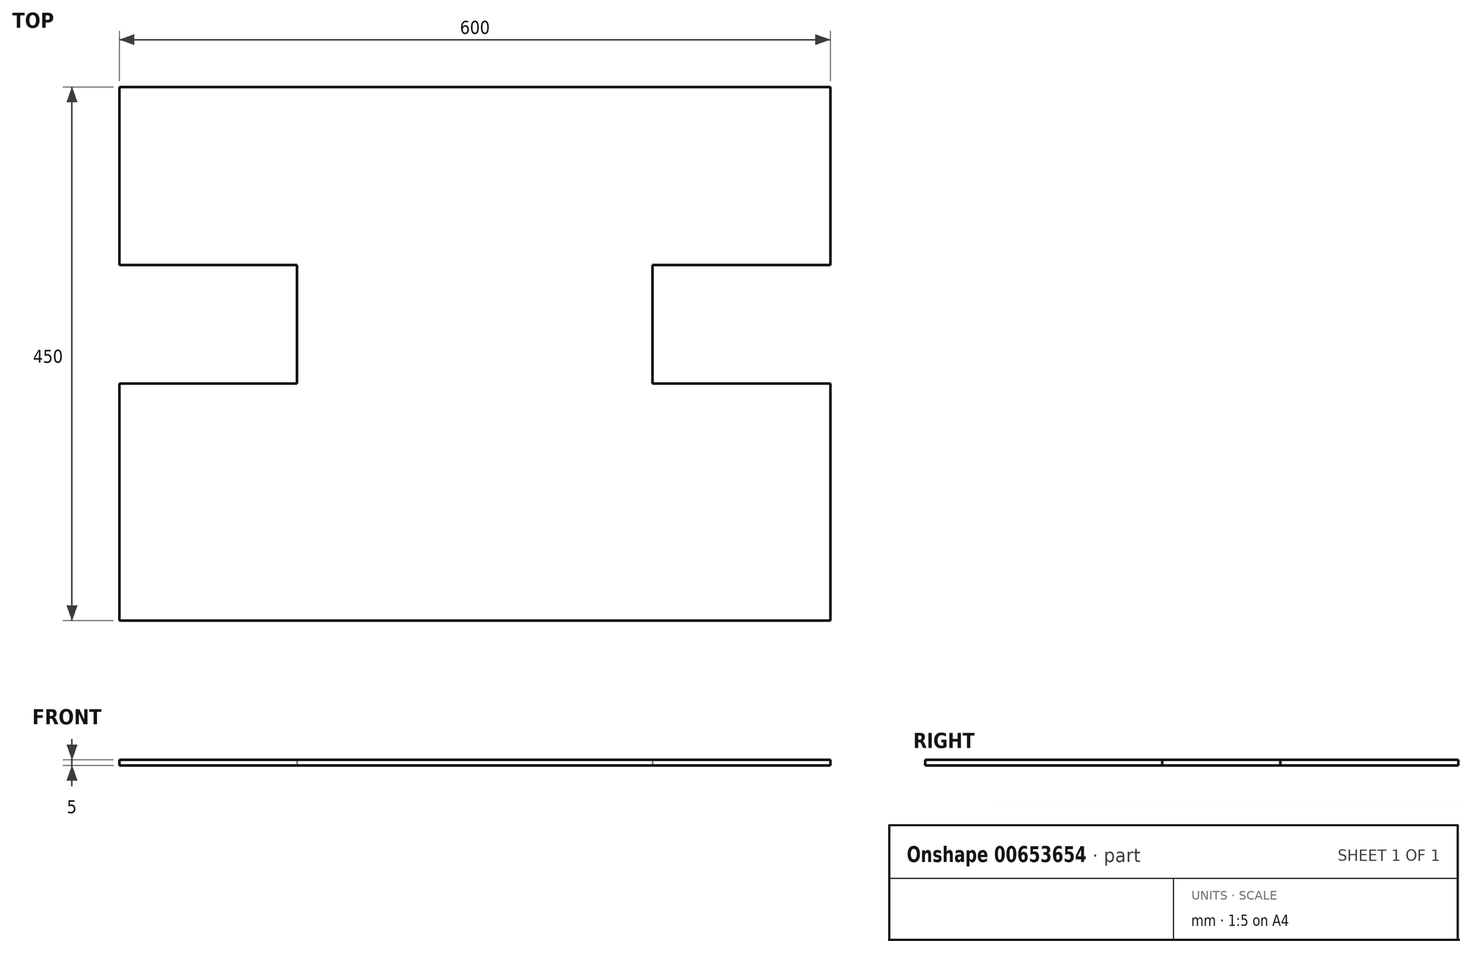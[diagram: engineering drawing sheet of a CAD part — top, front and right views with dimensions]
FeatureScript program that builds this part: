
annotation { "Feature Type Name" : "Feature", "Feature Type Description" : "" }
export const myFeature = defineFeature(function(context is Context, id is Id, definition is map)
    precondition{}
    {
        {
            var Q0;
            Q0=qCreatedBy(makeId("Top.planeOp"),FACE);
            var sketch = newSketch(context, id + "F0", { "sketchPlane" : qUnion([Q0])});
            skLineSegment(sketch, "E0.bottom", {"start": v(0, 0) * mm, "end": v(600, 0) * mm});
            skLineSegment(sketch, "E0.top", {"start": v(0, 450) * mm, "end": v(600, 450) * mm});
            skLineSegment(sketch, "E0.left", {"start": v(0, 0) * mm, "end": v(0, 450) * mm});
            skLineSegment(sketch, "E0.right", {"start": v(600, 0) * mm, "end": v(600, 450) * mm});
            skLineSegment(sketch, "E1", {"start": v(0, 0) * mm, "end": v(150, -200) * mm});
            skLineSegment(sketch, "E2", {"start": v(150, -200) * mm, "end": v(450, -200) * mm});
            skLineSegment(sketch, "E3", {"start": v(450, -200) * mm, "end": v(600, 0) * mm});
            skLineSegment(sketch, "E4.bottom", {"start": v(0, 300) * mm, "end": v(150, 300) * mm});
            skLineSegment(sketch, "E4.top", {"start": v(0, 200) * mm, "end": v(150, 200) * mm});
            skLineSegment(sketch, "E4.left", {"start": v(0, 300) * mm, "end": v(0, 200) * mm});
            skLineSegment(sketch, "E4.right", {"start": v(150, 300) * mm, "end": v(150, 200) * mm});
            skLineSegment(sketch, "E5.bottom", {"start": v(600, 200) * mm, "end": v(450, 200) * mm});
            skLineSegment(sketch, "E5.top", {"start": v(600, 300) * mm, "end": v(450, 300) * mm});
            skLineSegment(sketch, "E5.left", {"start": v(600, 200) * mm, "end": v(600, 300) * mm});
            skLineSegment(sketch, "E5.right", {"start": v(450, 200) * mm, "end": v(450, 300) * mm});
            skSolve(sketch);
        }
        {
            var Q0;
            {var subQ6=sQuery(id+"F0.wireOp",EDGE,"E0.bottom");Q0=makeQuery(id+"F0.imprint","IMPRINT",FACE,{"disambiguationData":[TD([[makeQuery(id+"F0.imprint","IMPRINT",EDGE,{"derivedFrom":subQ6}),1.0]])]});}
            var Q1;
            Q1=makeQuery(id+"F0.imprint","IMPRINT",FACE,{"disambiguationData":[TD([[makeQuery(id+"F0.imprint","IMPRINT",EDGE,{"derivedFrom":sQuery(id+"F0.wireOp",EDGE,"E0.bottom")}),-1.0]])]});
            extrude(context, id + "F1", {"entities" : qUnion([Q0, Q1]), "depth" : 5 * mm, "offsetDistance" : 25 * mm});
        }
        {
            var Q0;
            Q0=makeQuery(id+"F1.opExtrude","CAP_FACE",FACE,{"disambiguationData":[OSD([sQuery(id+"F0.wireOp",EDGE,"E0.top"),sQuery(id+"F0.wireOp",EDGE,"E0.left"),sQuery(id+"F0.wireOp",EDGE,"E0.right"),sQuery(id+"F0.wireOp",EDGE,"E1"),sQuery(id+"F0.wireOp",EDGE,"E2"),sQuery(id+"F0.wireOp",EDGE,"E3"),sQuery(id+"F0.wireOp",EDGE,"E4.bottom"),sQuery(id+"F0.wireOp",EDGE,"E4.top"),sQuery(id+"F0.wireOp",EDGE,"E4.right"),sQuery(id+"F0.wireOp",EDGE,"E5.bottom"),sQuery(id+"F0.wireOp",EDGE,"E5.top"),sQuery(id+"F0.wireOp",EDGE,"E5.right")])],"isStart":false});
            var sketch = newSketch(context, id + "F2", { "sketchPlane" : qUnion([Q0])});
            skLineSegment(sketch, "E6.bottom", {"start": v(0, 0) * mm, "end": v(635.92, 0) * mm});
            skLineSegment(sketch, "E6.top", {"start": v(0, -207.59) * mm, "end": v(635.92, -207.59) * mm});
            skLineSegment(sketch, "E6.left", {"start": v(0, 0) * mm, "end": v(0, -207.59) * mm});
            skLineSegment(sketch, "E6.right", {"start": v(635.92, 0) * mm, "end": v(635.92, -207.59) * mm});
            skSolve(sketch);
        }
        {
            var Q0;
            Q0 = qSketchRegion(id + "F2", true);
            extrude(context, id + "F3", {"entities" : qUnion([Q0]), "operationType" : NewBodyOperationType.REMOVE, "oppositeDirection" : true, "depth" : 25 * mm, "offsetDistance" : 25 * mm});
        }
    });
